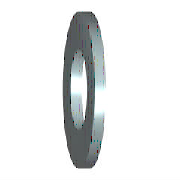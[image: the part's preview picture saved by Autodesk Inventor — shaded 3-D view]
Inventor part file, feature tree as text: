
AUTODESK INVENTOR PART (.ipt)
format: ipt  version: 2020 (Build 240168000, 168)  size: 109,568 bytes
history: native  units: mm (DEFAULTED — no unit token found)
features: other x1, plane x1, sketch x1
ambient origin geometry x7: Origin, YZ Plane, XY Plane, X Axis, Y Axis, Z Axis, Center Point
bodies: Solid1 (feature_tree), Body (feature_tree)
feature tree (3):
  other  "Work Axis1"
  plane  "Work Plane1"
  sketch  "Sketch"  dims[d0=4.3mm d1=9.0mm d2=0.8mm d3=0.0mm d4=0.0mm d5=0.0mm d6=0.0mm d7=0.0mm]
